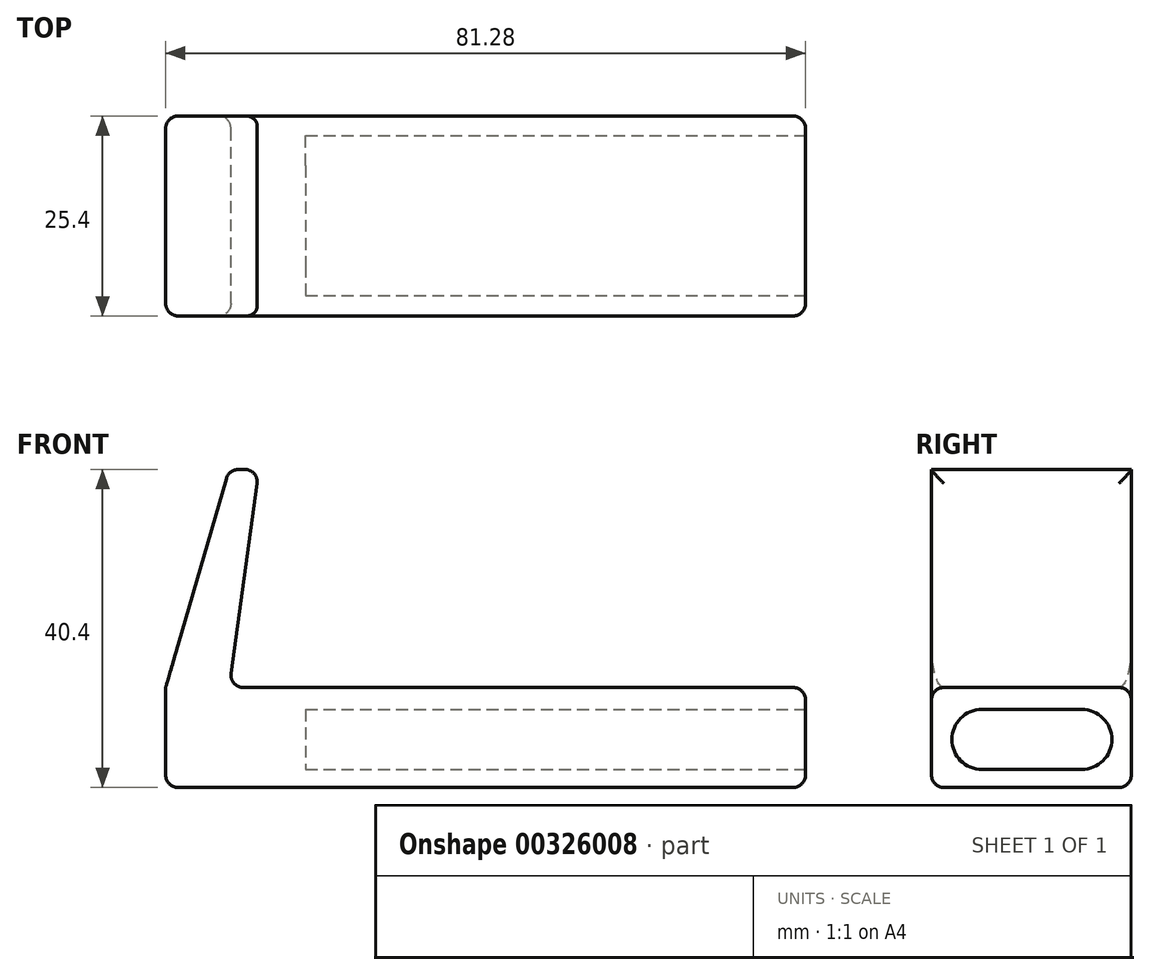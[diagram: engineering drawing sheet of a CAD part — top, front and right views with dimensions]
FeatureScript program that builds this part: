
annotation { "Feature Type Name" : "Feature", "Feature Type Description" : "" }
export const myFeature = defineFeature(function(context is Context, id is Id, definition is map)
    precondition{}
    {
        {
            var Q0;
            Q0=qCreatedBy(makeId("Front.planeOp"),FACE);
            var sketch = newSketch(context, id + "F0", { "sketchPlane" : qUnion([Q0])});
            skLineSegment(sketch, "E0", {"start": v(32.67, -0.15) * mm, "end": v(-45.46, -0.15) * mm});
            skLineSegment(sketch, "E1", {"start": v(-47.04, 1.43) * mm, "end": v(-47.04, 12.55) * mm});
            skLineSegment(sketch, "E2", {"start": v(-47.04, 12.55) * mm, "end": v(-38.98, 40.25) * mm});
            skLineSegment(sketch, "E3", {"start": v(-38.98, 40.25) * mm, "end": v(-35.17, 40.25) * mm});
            skLineSegment(sketch, "E4", {"start": v(-35.17, 40.25) * mm, "end": v(-38.73, 14.34) * mm});
            skLineSegment(sketch, "E5", {"start": v(-37.17, 12.55) * mm, "end": v(32.67, 12.55) * mm});
            skLineSegment(sketch, "E6", {"start": v(34.24, 10.98) * mm, "end": v(34.24, 1.43) * mm});
            skPoint(sketch, "E7.visualSharp", {"position": v(-38.98, 12.55) * mm});
            skArc(sketch, "E7.filletArc", {"start": v(-38.73, 14.34) * mm, "mid": v(-38.36, 13.1) * mm, "end": v(-37.17, 12.55) * mm});
            skPoint(sketch, "E8.visualSharp", {"position": v(-47.04, -0.15) * mm});
            skArc(sketch, "E8.filletArc", {"start": v(-47.04, 1.43) * mm, "mid": v(-46.57, 0.32) * mm, "end": v(-45.46, -0.15) * mm});
            skPoint(sketch, "E9.visualSharp", {"position": v(34.24, -0.15) * mm});
            skArc(sketch, "E9.filletArc", {"start": v(32.67, -0.15) * mm, "mid": v(33.78, 0.32) * mm, "end": v(34.24, 1.43) * mm});
            skPoint(sketch, "E10.visualSharp", {"position": v(34.24, 12.55) * mm});
            skArc(sketch, "E10.filletArc", {"start": v(34.24, 10.98) * mm, "mid": v(33.78, 12.1) * mm, "end": v(32.67, 12.55) * mm});
            skSolve(sketch);
        }
        {
            var Q0;
            Q0=makeQuery(id+"F0.imprint","IMPRINT",FACE,{"disambiguationData":[TD([[makeQuery(id+"F0.imprint","IMPRINT",EDGE,{"derivedFrom":sQuery(id+"F0.wireOp",EDGE,"E0")}),-1.0]])]});
            extrude(context, id + "F1", {"entities" : qUnion([Q0]), "depth" : 25.4 * mm});
        }
        {
            var Q0;
            Q0=makeQuery(id+"F1.opExtrude","CAP_EDGE",EDGE,{"disambiguationData":[OSD([sQuery(id+"F0.wireOp",EDGE,"E5")])],"isStart":false});
            var Q1;
            Q1=makeQuery(id+"F1.opExtrude","CAP_EDGE",EDGE,{"disambiguationData":[OSD([sQuery(id+"F0.wireOp",EDGE,"E5")])],"isStart":true});
            var Q2;
            Q2=makeQuery(id+"F1.opExtrude","SWEPT_EDGE",EDGE,{"disambiguationData":[OSD([sQuery(id+"F0.wireOp",EDGE,"E3"),sQuery(id+"F0.wireOp",EDGE,"E4")])]});
            var Q3;
            Q3=makeQuery(id+"F1.opExtrude","SWEPT_EDGE",EDGE,{"disambiguationData":[OSD([sQuery(id+"F0.wireOp",EDGE,"E2"),sQuery(id+"F0.wireOp",EDGE,"E3")])]});
            fillet(context, id + "F2", {"entities" : qUnion([Q0, Q1, Q2, Q3]), "radius" : 1.57 * mm, "tangentPropagation" : true, "allowEdgeOverflow" : false});
        }
        {
            var Q0;
            Q0=makeQuery(id+"F1.opExtrude","SWEPT_FACE",FACE,{"disambiguationData":[OSD([sQuery(id+"F0.wireOp",EDGE,"E6")])]});
            var sketch = newSketch(context, id + "F3", { "sketchPlane" : qUnion([Q0])});
            skLineSegment(sketch, "E11.bottom", {"start": v(-6.3, 9.76) * mm, "end": v(-19, 9.76) * mm});
            skLineSegment(sketch, "E11.top", {"start": v(-6.3, 2.14) * mm, "end": v(-19, 2.14) * mm});
            skLineSegment(sketch, "E11.left", {"start": v(-2.48, 5.95) * mm, "end": v(-2.48, 5.95) * mm});
            skLineSegment(sketch, "E11.right", {"start": v(-22.8, 5.95) * mm, "end": v(-22.8, 5.95) * mm});
            skPoint(sketch, "E11.middle", {"position": v(-12.64, 5.95) * mm});
            skPoint(sketch, "E12.visualSharp", {"position": v(-22.8, 2.14) * mm});
            skArc(sketch, "E12.filletArc", {"start": v(-22.8, 5.95) * mm, "mid": v(-21.69, 3.26) * mm, "end": v(-19, 2.14) * mm});
            skPoint(sketch, "E13.visualSharp", {"position": v(-22.8, 9.76) * mm});
            skArc(sketch, "E13.filletArc", {"start": v(-19, 9.76) * mm, "mid": v(-21.69, 8.64) * mm, "end": v(-22.8, 5.95) * mm});
            skPoint(sketch, "E14.visualSharp", {"position": v(-2.48, 9.76) * mm});
            skArc(sketch, "E14.filletArc", {"start": v(-2.48, 5.95) * mm, "mid": v(-3.6, 8.64) * mm, "end": v(-6.3, 9.76) * mm});
            skPoint(sketch, "E15.visualSharp", {"position": v(-2.48, 2.14) * mm});
            skArc(sketch, "E15.filletArc", {"start": v(-6.3, 2.14) * mm, "mid": v(-3.6, 3.26) * mm, "end": v(-2.48, 5.95) * mm});
            skSolve(sketch);
        }
        {
            var Q0;
            Q0=makeQuery(id+"F3.imprint","IMPRINT",FACE,{"disambiguationData":[TD([[makeQuery(id+"F3.imprint","IMPRINT",EDGE,{"derivedFrom":sQuery(id+"F3.wireOp",EDGE,"E11.bottom")}),1.0]])]});
            extrude(context, id + "F4", {"entities" : qUnion([Q0]), "operationType" : NewBodyOperationType.REMOVE, "oppositeDirection" : true, "depth" : 63.5 * mm});
        }
    });
